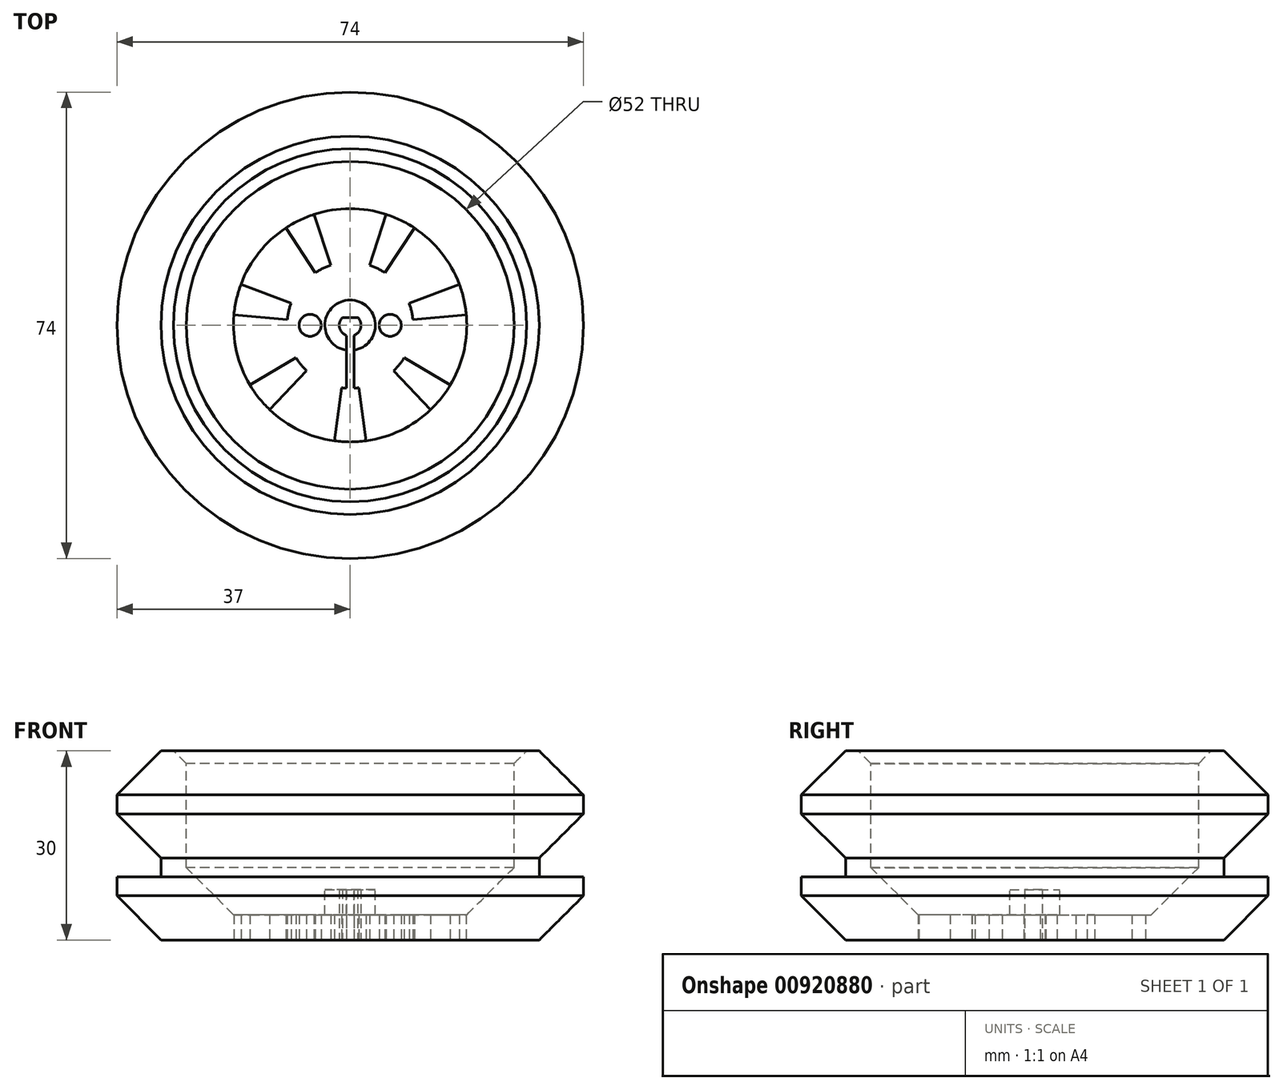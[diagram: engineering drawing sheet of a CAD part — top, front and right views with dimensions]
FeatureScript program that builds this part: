
annotation { "Feature Type Name" : "Feature", "Feature Type Description" : "" }
export const myFeature = defineFeature(function(context is Context, id is Id, definition is map)
    precondition{}
    {
        {
            var Q0;
            Q0=qCreatedBy(makeId("Front.planeOp"),FACE);
            var sketch = newSketch(context, id + "F0", { "sketchPlane" : qUnion([Q0])});
            skLineSegment(sketch, "E0", {"start": v(0, 0) * mm, "end": v(-30, 0) * mm});
            skLineSegment(sketch, "E1", {"start": v(-30, 0) * mm, "end": v(-37, 7) * mm});
            skLineSegment(sketch, "E2", {"start": v(-37, 7) * mm, "end": v(-37, 10) * mm});
            skLineSegment(sketch, "E3", {"start": v(-37, 10) * mm, "end": v(-30, 10) * mm});
            skLineSegment(sketch, "E4", {"start": v(-30, 10) * mm, "end": v(-30, 13) * mm});
            skLineSegment(sketch, "E5", {"start": v(-30, 13) * mm, "end": v(-37, 20) * mm});
            skLineSegment(sketch, "E6", {"start": v(-37, 20) * mm, "end": v(-37, 23) * mm});
            skLineSegment(sketch, "E7", {"start": v(0, 4) * mm, "end": v(0, 0) * mm});
            skLineSegment(sketch, "E8", {"start": v(-26, 28) * mm, "end": v(-26, 11.5) * mm});
            skLineSegment(sketch, "E9", {"start": v(-18.5, 4) * mm, "end": v(0, 4) * mm});
            skLineSegment(sketch, "E10", {"start": v(-37, 23) * mm, "end": v(-30, 30) * mm});
            skLineSegment(sketch, "E11", {"start": v(-30, 30) * mm, "end": v(-28, 30) * mm});
            skLineSegment(sketch, "E12", {"start": v(-28, 30) * mm, "end": v(-26, 28) * mm});
            skLineSegment(sketch, "E13", {"start": v(-18.5, 4) * mm, "end": v(-26, 11.5) * mm});
            skLineSegment(sketch, "E14", {"start": v(0, 4) * mm, "end": v(0, 8) * mm});
            skLineSegment(sketch, "E15", {"start": v(0, 8) * mm, "end": v(-4, 8) * mm});
            skLineSegment(sketch, "E16", {"start": v(-4, 8) * mm, "end": v(-4, 4) * mm});
            skSolve(sketch);
        }
        {
            var Q0;
            Q0=makeQuery(id+"F0.imprint","IMPRINT",FACE,{"disambiguationData":[TD([[makeQuery(id+"F0.imprint","IMPRINT",EDGE,{"derivedFrom":sQuery(id+"F0.wireOp",EDGE,"E0")}),-1.0]])]});
            var Q1;
            {var subQ0=sQuery(id+"F0.wireOp",EDGE,"E14");Q1=makeQuery(id+"F0.imprint","IMPRINT",FACE,{"disambiguationData":[TD([[makeQuery(id+"F0.imprint","IMPRINT",EDGE,{"derivedFrom":subQ0}),1.0]])]});}
            var Q2;
            Q2=sQuery(id+"F0.wireOp",EDGE,"E7");
            revolve(context, id + "F1", {"surfaceOperationType" : NewSurfaceOperationType.NEW, "entities" : qUnion([Q0, Q1]), "axis" : qUnion([Q2]), "revolveType" : RevolveType.FULL});
        }
        {
            var Q0;
            Q0=qCreatedBy(makeId("Top.planeOp"),FACE);
            var sketch = newSketch(context, id + "F2", { "sketchPlane" : qUnion([Q0])});
            skCircle(sketch, "E17", {"center": v(0, 0) * mm, "radius": 1.73 * mm});
            skLineSegment(sketch, "E18", {"start": v(-1.21, 1.23) * mm, "end": v(1.21, 1.23) * mm});
            skCircle(sketch, "E19", {"center": v(6.35, 0) * mm, "radius": 1.75 * mm});
            skCircle(sketch, "E20", {"center": v(-6.35, 0) * mm, "radius": 1.75 * mm});
            skLineSegment(sketch, "E21", {"start": v(-6.35, 0) * mm, "end": v(0, 0) * mm, "construction": true});
            skLineSegment(sketch, "E22", {"start": v(0, 0) * mm, "end": v(6.35, 0) * mm, "construction": true});
            skCircle(sketch, "E23.0", {"center": v(0, 0) * mm, "radius": 18.5 * mm});
            skLineSegment(sketch, "E24", {"start": v(-0.6, -9.98) * mm, "end": v(-0.6, -1.62) * mm});
            skLineSegment(sketch, "E25", {"start": v(0.6, -9.98) * mm, "end": v(0.6, -1.62) * mm});
            skLineSegment(sketch, "E26", {"start": v(-1.35, -9.9) * mm, "end": v(-2.5, -18.33) * mm});
            skLineSegment(sketch, "E27", {"start": v(2.5, -18.33) * mm, "end": v(1.35, -9.9) * mm});
            skLineSegment(sketch, "E28", {"start": v(12.77, -13.38) * mm, "end": v(6.9, -7.23) * mm});
            skLineSegment(sketch, "E29", {"start": v(18.43, 1.64) * mm, "end": v(9.96, 0.89) * mm});
            skLineSegment(sketch, "E30", {"start": v(15.89, -9.47) * mm, "end": v(8.59, -5.12) * mm});
            skLineSegment(sketch, "E31", {"start": v(9.36, 3.52) * mm, "end": v(17.31, 6.52) * mm});
            skLineSegment(sketch, "E32", {"start": v(5.52, 8.34) * mm, "end": v(10.2, 15.43) * mm});
            skLineSegment(sketch, "E33", {"start": v(3.08, 9.51) * mm, "end": v(5.7, 17.6) * mm});
            skLineSegment(sketch, "E34", {"start": v(-3.08, 9.51) * mm, "end": v(-5.7, 17.6) * mm});
            skLineSegment(sketch, "E35", {"start": v(-5.52, 8.34) * mm, "end": v(-10.2, 15.43) * mm});
            skLineSegment(sketch, "E36", {"start": v(-9.36, 3.52) * mm, "end": v(-17.31, 6.52) * mm});
            skLineSegment(sketch, "E37", {"start": v(-9.96, 0.89) * mm, "end": v(-18.43, 1.64) * mm});
            skLineSegment(sketch, "E38", {"start": v(-8.59, -5.12) * mm, "end": v(-15.89, -9.47) * mm});
            skLineSegment(sketch, "E39", {"start": v(-6.9, -7.23) * mm, "end": v(-12.77, -13.38) * mm});
            skLineSegment(sketch, "E40", {"start": v(-15.89, -9.47) * mm, "end": v(-18.43, 1.64) * mm, "construction": true});
            skLineSegment(sketch, "E41", {"start": v(-17.31, 6.52) * mm, "end": v(-10.2, 15.43) * mm, "construction": true});
            skLineSegment(sketch, "E42", {"start": v(-5.7, 17.6) * mm, "end": v(5.7, 17.6) * mm, "construction": true});
            skLineSegment(sketch, "E43", {"start": v(10.2, 15.43) * mm, "end": v(17.31, 6.52) * mm, "construction": true});
            skLineSegment(sketch, "E44", {"start": v(18.43, 1.64) * mm, "end": v(15.89, -9.47) * mm, "construction": true});
            skLineSegment(sketch, "E45", {"start": v(12.77, -13.38) * mm, "end": v(2.5, -18.33) * mm, "construction": true});
            skLineSegment(sketch, "E46", {"start": v(-2.5, -18.33) * mm, "end": v(-12.77, -13.38) * mm, "construction": true});
            skArc(sketch, "E47", {"start": v(-8.59, -5.12) * mm, "mid": v(-7.82, -6.23) * mm, "end": v(-6.9, -7.23) * mm});
            skArc(sketch, "E48", {"start": v(-6.9, -7.23) * mm, "mid": v(-4.34, -9) * mm, "end": v(-1.35, -9.9) * mm, "construction": true});
            skArc(sketch, "E49", {"start": v(-1.35, -9.9) * mm, "mid": v(-0.98, -9.95) * mm, "end": v(-0.6, -9.98) * mm});
            skArc(sketch, "E50", {"start": v(-9.96, 0.89) * mm, "mid": v(-9.75, -2.23) * mm, "end": v(-8.59, -5.12) * mm, "construction": true});
            skArc(sketch, "E51", {"start": v(-9.36, 3.52) * mm, "mid": v(-9.75, 2.23) * mm, "end": v(-9.96, 0.89) * mm});
            skArc(sketch, "E52", {"start": v(-5.52, 8.34) * mm, "mid": v(-7.82, 6.23) * mm, "end": v(-9.36, 3.52) * mm, "construction": true});
            skArc(sketch, "E53", {"start": v(-3.08, 9.51) * mm, "mid": v(-4.34, 9) * mm, "end": v(-5.52, 8.34) * mm});
            skArc(sketch, "E54", {"start": v(3.08, 9.51) * mm, "mid": v(0, 10) * mm, "end": v(-3.08, 9.51) * mm, "construction": true});
            skArc(sketch, "E55", {"start": v(5.52, 8.34) * mm, "mid": v(4.34, 9) * mm, "end": v(3.08, 9.51) * mm});
            skArc(sketch, "E56", {"start": v(9.36, 3.52) * mm, "mid": v(7.82, 6.23) * mm, "end": v(5.52, 8.34) * mm, "construction": true});
            skArc(sketch, "E57", {"start": v(9.96, 0.89) * mm, "mid": v(9.75, 2.23) * mm, "end": v(9.36, 3.52) * mm});
            skArc(sketch, "E58", {"start": v(8.59, -5.12) * mm, "mid": v(9.75, -2.23) * mm, "end": v(9.96, 0.89) * mm, "construction": true});
            skArc(sketch, "E59", {"start": v(6.9, -7.23) * mm, "mid": v(7.82, -6.23) * mm, "end": v(8.59, -5.12) * mm});
            skArc(sketch, "E60", {"start": v(1.35, -9.9) * mm, "mid": v(4.34, -9) * mm, "end": v(6.9, -7.23) * mm, "construction": true});
            skArc(sketch, "E61", {"start": v(-0.6, -9.98) * mm, "mid": v(0, -10) * mm, "end": v(0.6, -9.98) * mm, "construction": true});
            skArc(sketch, "E62", {"start": v(0.6, -9.98) * mm, "mid": v(0.98, -9.95) * mm, "end": v(1.35, -9.9) * mm});
            skSolve(sketch);
        }
        {
            var Q0;
            {var subQ0=sQuery(id+"F2.wireOp",EDGE,"E36");Q0=makeQuery(id+"F2.imprint","IMPRINT",FACE,{"disambiguationData":[TD([[makeQuery(id+"F2.imprint","IMPRINT",EDGE,{"derivedFrom":subQ0}),1.0]])]});}
            var Q1;
            {var subQ0=sQuery(id+"F2.wireOp",EDGE,"E38");Q1=makeQuery(id+"F2.imprint","IMPRINT",FACE,{"disambiguationData":[TD([[makeQuery(id+"F2.imprint","IMPRINT",EDGE,{"derivedFrom":subQ0}),1.0]])]});}
            var Q2;
            {var subQ0=sQuery(id+"F2.wireOp",EDGE,"E24");Q2=makeQuery(id+"F2.imprint","IMPRINT",FACE,{"disambiguationData":[TD([[makeQuery(id+"F2.imprint","IMPRINT",EDGE,{"derivedFrom":subQ0}),-1.0]])]});}
            var Q3;
            {var subQ0=sQuery(id+"F2.wireOp",EDGE,"E28");Q3=makeQuery(id+"F2.imprint","IMPRINT",FACE,{"disambiguationData":[TD([[makeQuery(id+"F2.imprint","IMPRINT",EDGE,{"derivedFrom":subQ0}),-1.0]])]});}
            var Q4;
            {var subQ0=sQuery(id+"F2.wireOp",EDGE,"E29");Q4=makeQuery(id+"F2.imprint","IMPRINT",FACE,{"disambiguationData":[TD([[makeQuery(id+"F2.imprint","IMPRINT",EDGE,{"derivedFrom":subQ0}),-1.0]])]});}
            var Q5;
            {var subQ0=sQuery(id+"F2.wireOp",EDGE,"E32");Q5=makeQuery(id+"F2.imprint","IMPRINT",FACE,{"disambiguationData":[TD([[makeQuery(id+"F2.imprint","IMPRINT",EDGE,{"derivedFrom":subQ0}),1.0]])]});}
            var Q6;
            {var subQ0=sQuery(id+"F2.wireOp",EDGE,"E34");Q6=makeQuery(id+"F2.imprint","IMPRINT",FACE,{"disambiguationData":[TD([[makeQuery(id+"F2.imprint","IMPRINT",EDGE,{"derivedFrom":subQ0}),1.0]])]});}
            var Q7;
            Q7=makeQuery(id+"F2.imprint","IMPRINT",FACE,{"disambiguationData":[TD([[makeQuery(id+"F2.imprint","IMPRINT",EDGE,{"derivedFrom":sQuery(id+"F2.wireOp",EDGE,"E20")}),1.0]])]});
            var Q8;
            Q8=makeQuery(id+"F2.imprint","IMPRINT",FACE,{"disambiguationData":[TD([[makeQuery(id+"F2.imprint","IMPRINT",EDGE,{"derivedFrom":sQuery(id+"F2.wireOp",EDGE,"E19")}),1.0]])]});
            var Q9;
            {var subQ0=sQuery(id+"F2.wireOp",EDGE,"E18");Q9=makeQuery(id+"F2.imprint","IMPRINT",FACE,{"disambiguationData":[TD([[makeQuery(id+"F2.imprint","IMPRINT",EDGE,{"derivedFrom":subQ0}),-1.0]])]});}
            var Q10;
            Q10=makeQuery(id+"F1.opRevolve","SWEPT_FACE",FACE,{"disambiguationData":[OSD([sQuery(id+"F0.wireOp",EDGE,"E15")])]});
            extrude(context, id + "F3", {"entities" : qUnion([Q0, Q1, Q2, Q3, Q4, Q5, Q6, Q7, Q8, Q9]), "operationType" : NewBodyOperationType.REMOVE, "endBound" : BoundingType.UP_TO_SURFACE, "depth" : 25 * mm, "endBoundEntityFace" : qUnion([Q10]), "offsetDistance" : 25 * mm});
        }
    });
